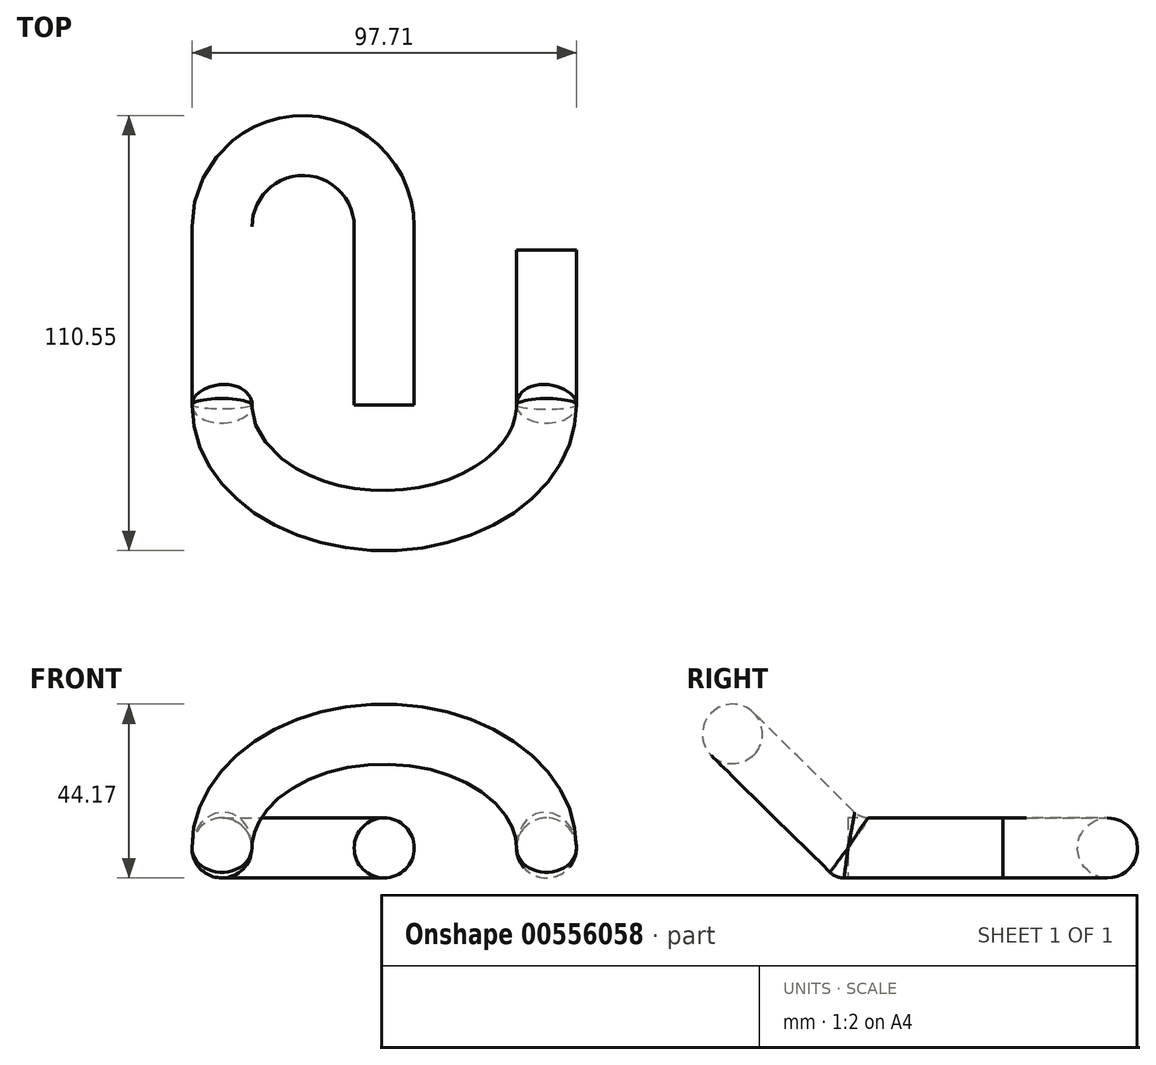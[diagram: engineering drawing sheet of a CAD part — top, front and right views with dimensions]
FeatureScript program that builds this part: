
annotation { "Feature Type Name" : "Feature", "Feature Type Description" : "" }
export const myFeature = defineFeature(function(context is Context, id is Id, definition is map)
    precondition{}
    {
        {
            var Q0;
            Q0=qCreatedBy(makeId("Top.planeOp"),FACE);
            var sketch = newSketch(context, id + "F0", { "sketchPlane" : qUnion([Q0])});
            skArc(sketch, "E0", {"start": v(20.62, 0) * mm, "mid": v(0, 20.62) * mm, "end": v(-20.62, 0) * mm});
            skLineSegment(sketch, "E1", {"start": v(-20.62, 0) * mm, "end": v(-20.62, -45.3) * mm});
            skLineSegment(sketch, "E2", {"start": v(20.62, 0) * mm, "end": v(20.62, -45.3) * mm});
            skSolve(sketch);
        }
        {
            var Q0;
            Q0=qCreatedBy(makeId("Right.planeOp"),FACE);
            var sketch = newSketch(context, id + "F1", { "sketchPlane" : qUnion([Q0])});
            skLineSegment(sketch, "E3.0", {"start": v(0, 0) * mm, "end": v(-45.3, 0) * mm, "construction": true});
            skLineSegment(sketch, "E4", {"start": v(-45.3, 0) * mm, "end": v(-78.4, 32.58) * mm, "construction": true});
            skSolve(sketch);
        }
        {
            var Q0;
            Q0=sQuery(id+"F0.wireOp",VERTEX,"E1.end");
            var Q1;
            Q1=sQuery(id+"F0.wireOp",VERTEX,"E2.end");
            var Q2;
            Q2=sQuery(id+"F1.wireOp",VERTEX,"E4.end");
            cPlane(context, id + "F2", {"entities" : qUnion([Q0, Q1, Q2]), "cplaneType" : CPlaneType.THREE_POINT, "offset" : 25.4 * mm, "width" : 152.4 * mm, "height" : 152.4 * mm});
        }
        {
            var Q0;
            Q0=qCreatedBy(id+"F2.planeOp",FACE);
            var sketch = newSketch(context, id + "F3", { "sketchPlane" : qUnion([Q0])});
            skPoint(sketch, "E5.0", {"position": v(20.62, -32.29) * mm});
            skPoint(sketch, "E6.0", {"position": v(-20.62, -32.29) * mm});
            skArc(sketch, "E7", {"start": v(-20.62, -32.29) * mm, "mid": v(20.62, -73.52) * mm, "end": v(61.85, -32.29) * mm});
            skLineSegment(sketch, "E8", {"start": v(-20.62, -32.29) * mm, "end": v(61.85, -32.29) * mm, "construction": true});
            skSolve(sketch);
        }
        {
            var Q0;
            Q0=qCreatedBy(makeId("Top.planeOp"),FACE);
            var sketch = newSketch(context, id + "F4", { "sketchPlane" : qUnion([Q0])});
            skPoint(sketch, "E9.0", {"position": v(61.85, -45.3) * mm});
            skLineSegment(sketch, "E10", {"start": v(61.85, -45.3) * mm, "end": v(61.85, -6) * mm});
            skSolve(sketch);
        }
        {
            var Q0;
            Q0=sQuery(id+"F4.wireOp",VERTEX,"E10.end");
            var Q1;
            Q1=sQuery(id+"F4.wireOp",EDGE,"E10");
            cPlane(context, id + "F5", {"entities" : qUnion([Q0, Q1]), "cplaneType" : CPlaneType.LINE_POINT, "offset" : 25.4 * mm, "width" : 152.4 * mm, "height" : 152.4 * mm});
        }
        {
            var Q0;
            Q0=qCreatedBy(id+"F5.planeOp",FACE);
            var sketch = newSketch(context, id + "F6", { "sketchPlane" : qUnion([Q0])});
            skPoint(sketch, "E11.0", {"position": v(-61.85, 0) * mm});
            skCircle(sketch, "E12", {"center": v(-61.85, 0) * mm, "radius": 7.62 * mm});
            skSolve(sketch);
        }
        {
            var Q0;
            Q0=makeQuery(id+"F6.imprint","IMPRINT",FACE,{"disambiguationData":[TD([[makeQuery(id+"F6.imprint","IMPRINT",EDGE,{"derivedFrom":sQuery(id+"F6.wireOp",EDGE,"E12")}),1.0]])]});
            var Q1;
            Q1=sQuery(id+"F4.wireOp",EDGE,"E10");
            var Q2;
            Q2=sQuery(id+"F3.wireOp",EDGE,"E7");
            var Q3;
            Q3=sQuery(id+"F0.wireOp",EDGE,"E1");
            var Q4;
            Q4=sQuery(id+"F0.wireOp",EDGE,"E0");
            var Q5;
            Q5=sQuery(id+"F0.wireOp",EDGE,"E2");
            sweep(context, id + "F7", {"profiles" : qUnion([Q0]), "path" : qUnion([Q1, Q2, Q3, Q4, Q5])});
        }
        {
            var Q0;
            Q0=makeQuery(id+"F7.opSweep","MID_CAP_EDGE",EDGE,{"disambiguationData":[OSD([sQuery(id+"F0.wireOp",VERTEX,"E1.end"),sQuery(id+"F6.wireOp",EDGE,"E12")]),OD(0.0)],"capPos":2.0});
            var Q1;
            Q1=makeQuery(id+"F7.opSweep","MID_CAP_EDGE",EDGE,{"disambiguationData":[OSD([sQuery(id+"F0.wireOp",VERTEX,"E1.end"),sQuery(id+"F6.wireOp",EDGE,"E12")]),OD(1.0)],"capPos":2.0});
            var Q2;
            Q2=makeQuery(id+"F7.opSweep","MID_CAP_EDGE",EDGE,{"disambiguationData":[OSD([sQuery(id+"F3.wireOp",VERTEX,"E7.end"),sQuery(id+"F6.wireOp",EDGE,"E12")]),OD(0.0)],"capPos":1.0});
            var Q3;
            Q3=makeQuery(id+"F7.opSweep","MID_CAP_EDGE",EDGE,{"disambiguationData":[OSD([sQuery(id+"F3.wireOp",VERTEX,"E7.end"),sQuery(id+"F6.wireOp",EDGE,"E12")]),OD(1.0)],"capPos":1.0});
            fillet(context, id + "F8", {"entities" : qUnion([Q0, Q1, Q2, Q3]), "radius" : 5.08 * mm, "tangentPropagation" : true, "allowEdgeOverflow" : false});
        }
    });
